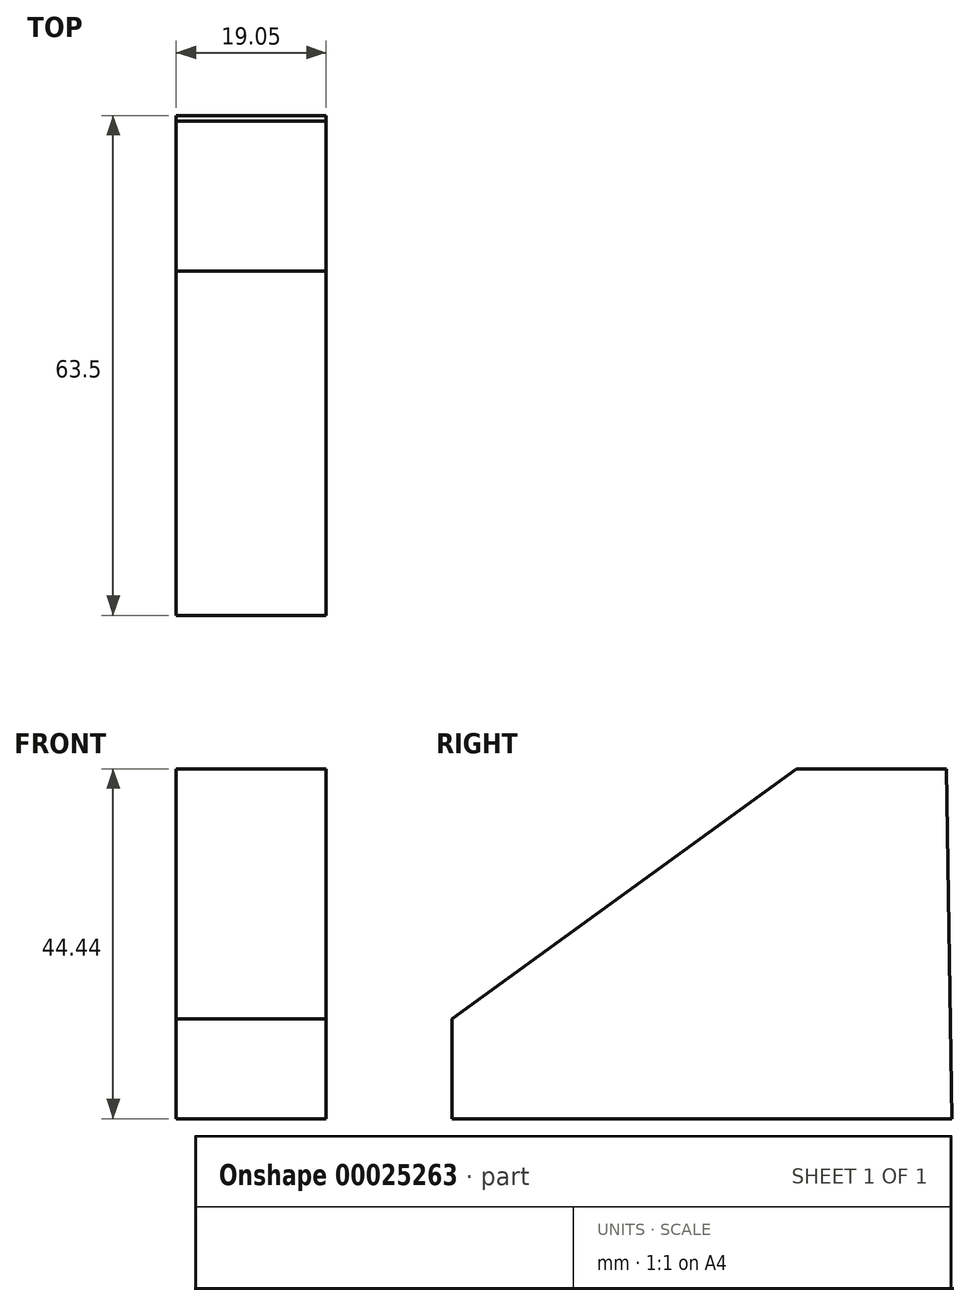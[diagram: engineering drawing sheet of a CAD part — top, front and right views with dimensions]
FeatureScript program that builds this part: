
annotation { "Feature Type Name" : "Feature", "Feature Type Description" : "" }
export const myFeature = defineFeature(function(context is Context, id is Id, definition is map)
    precondition{}
    {
        {
            var Q0;
            Q0=qCreatedBy(makeId("Right.planeOp"),FACE);
            var sketch = newSketch(context, id + "F0", { "sketchPlane" : qUnion([Q0])});
            skLineSegment(sketch, "E0", {"start": v(25.77, 42.75) * mm, "end": v(6.72, 42.75) * mm});
            skLineSegment(sketch, "E1", {"start": v(-37.02, -1.69) * mm, "end": v(26.48, -1.69) * mm});
            skLineSegment(sketch, "E2", {"start": v(26.48, -1.69) * mm, "end": v(25.77, 42.75) * mm});
            skLineSegment(sketch, "E3", {"start": v(-37.02, -1.69) * mm, "end": v(-37.02, 11.01) * mm});
            skLineSegment(sketch, "E4", {"start": v(-37.02, 11.01) * mm, "end": v(6.72, 42.75) * mm});
            skSolve(sketch);
        }
        {
            var Q0;
            Q0 = qSketchRegion(id + "F0", true);
            extrude(context, id + "F1", {"entities" : qUnion([Q0]), "depth" : 19.05 * mm});
        }
    });
